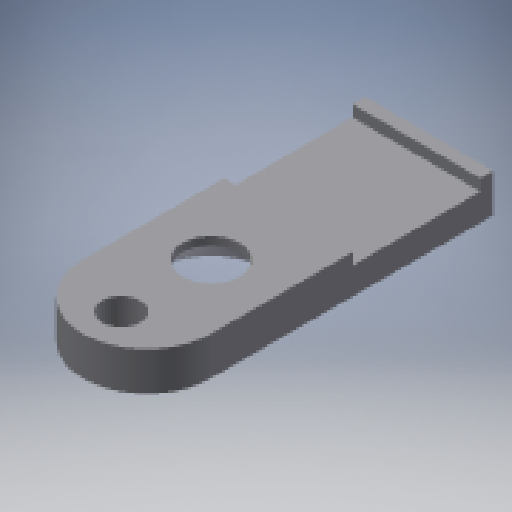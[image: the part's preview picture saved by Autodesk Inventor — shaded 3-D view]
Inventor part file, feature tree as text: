
AUTODESK INVENTOR PART (.ipt)
format: ipt  version: 2024.3 (Build 283343000, 343)  size: 256,512 bytes
history: native  units: mm
features: sketch x3, extrude x2, hole x2, projected_geometry x2
ambient origin geometry x8: Origin, YZ Plane, XZ Plane, XY Plane, X Axis, Y Axis, Z Axis, Center Point
bodies: Volumenkörper1 (feature_tree)
feature tree (9):
  extrude  "Extrusion1"  Depth=20.0mm
  extrude  "Extrusion2"  Depth=0.9mm
  hole  "Bohrung1"  [1 undecoded]
  hole  "Bohrung2"  [1 undecoded]
  sketch  "Skizze2"  dims[d0=10.0mm d1=20.0mm]
  projected_geometry  "Projizierte Kontur1"
  sketch  "Skizze4"  dims[d2=3.0mm d3=0.0mm d4=0.9mm]
  projected_geometry  "Projizierte Kontur2"
  sketch  "Skizze5"  dims[d5=0.5mm d6=10.0mm d7=0.0mm d8=0.0mm d9=5.0mm d10=4.5mm d11=8.0mm d12=9.2mm d13=2.0mm d14=90.0deg d15=8.0mm d16=20.594885mm d17=7.0mm d18=3.0mm d19=6.0mm d20=9.2mm d21=2.0mm d22=90.0deg d23=8.0mm d24=20.594885mm]
note: 2 required parameter values undecoded (feature->parameter linkage not recoverable at this tier; creation-order binding heuristic only, values carry confidence <= 0.55)
